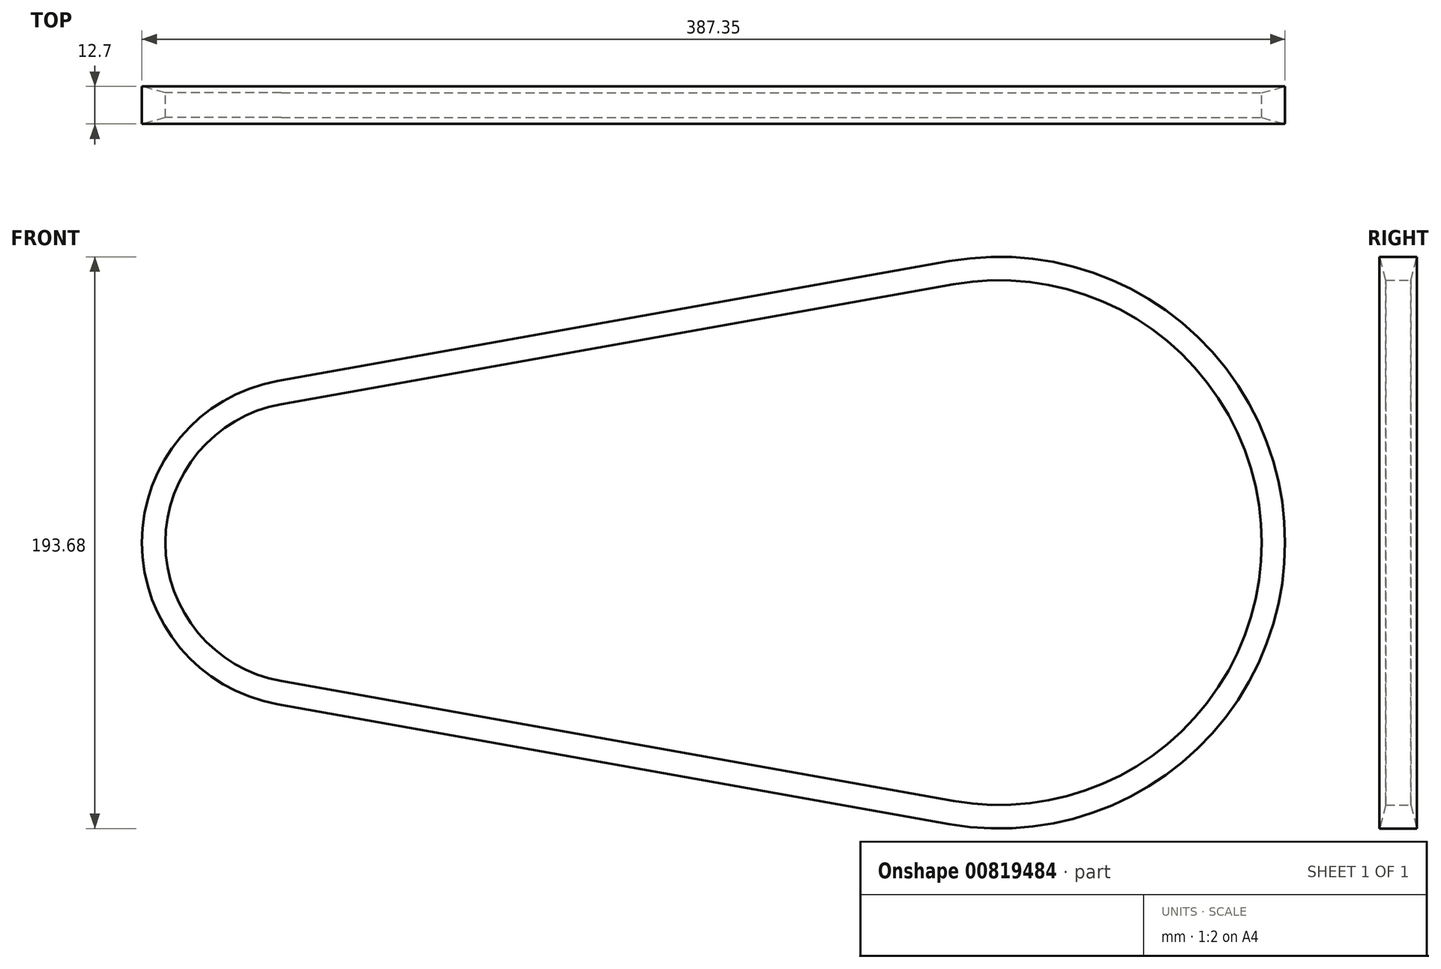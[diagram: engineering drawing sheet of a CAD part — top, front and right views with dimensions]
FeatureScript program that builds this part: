
annotation { "Feature Type Name" : "Feature", "Feature Type Description" : "" }
export const myFeature = defineFeature(function(context is Context, id is Id, definition is map)
    precondition{}
    {
        {
            var Q0;
            Q0=qCreatedBy(makeId("Front.planeOp"),FACE);
            var sketch = newSketch(context, id + "F0", { "sketchPlane" : qUnion([Q0])});
            skArc(sketch, "E0", {"start": v(-15.62, -87.52) * mm, "mid": v(88.9, 0) * mm, "end": v(-15.62, 87.52) * mm});
            skArc(sketch, "E1", {"start": v(-243.32, 46.88) * mm, "mid": v(-282.58, 0) * mm, "end": v(-243.32, -46.88) * mm});
            skLineSegment(sketch, "E2", {"start": v(-198.56, 30.72) * mm, "end": v(-176.73, 4.86) * mm, "construction": true});
            skLineSegment(sketch, "E3", {"start": v(-15.62, -87.52) * mm, "end": v(-243.32, -46.88) * mm});
            skArc(sketch, "E4", {"start": v(-176.73, 4.86) * mm, "mid": v(-154.6, -6.36) * mm, "end": v(-131.12, 1.71) * mm, "construction": true});
            skLineSegment(sketch, "E5.trimOffspring", {"start": v(-131.12, 1.71) * mm, "end": v(-59.4, 66.13) * mm, "construction": true});
            skLineSegment(sketch, "E6", {"start": v(-243.32, 46.88) * mm, "end": v(-15.62, 87.52) * mm});
            skSolve(sketch);
        }
        {
            var Q0;
            Q0=sQuery(id+"F0.wireOp",EDGE,"E3");
            cPoint(context, id + "F1", {"entities" : qUnion([Q0]), "parameter" : 0.5});
        }
        {
            var Q0;
            Q0=qCreatedBy(id+"F1",VERTEX);
            var Q1;
            Q1=sQuery(id+"F0.wireOp",EDGE,"E3");
            cPlane(context, id + "F2", {"entities" : qUnion([Q0, Q1]), "cplaneType" : CPlaneType.CURVE_POINT, "offset" : 25.4 * mm, "width" : 152.4 * mm, "height" : 152.4 * mm});
        }
        {
            var Q0;
            Q0=qCreatedBy(id+"F2.planeOp",FACE);
            var sketch = newSketch(context, id + "F3", { "sketchPlane" : qUnion([Q0])});
            skLineSegment(sketch, "E7", {"start": v(6.35, -96.84) * mm, "end": v(-6.35, -96.84) * mm});
            skLineSegment(sketch, "E8", {"start": v(-6.35, -96.84) * mm, "end": v(-4.22, -88.9) * mm});
            skLineSegment(sketch, "E9", {"start": v(-4.22, -88.9) * mm, "end": v(4.22, -88.9) * mm});
            skLineSegment(sketch, "E10", {"start": v(4.22, -88.9) * mm, "end": v(6.35, -96.84) * mm});
            skLineSegment(sketch, "E11", {"start": v(0, -88.9) * mm, "end": v(0, -96.84) * mm, "construction": true});
            skPoint(sketch, "E11.startSnap0", {"position": v(0, -96.84) * mm});
            skSolve(sketch);
        }
        {
            var Q0;
            Q0=qSketchRegion(id+"F3",true);
            var Q1;
            Q1=qConstructionFilter(qBodyType(qCreatedBy(id+"F0",EDGE),BodyType.WIRE),ConstructionObject.NO);
            sweep(context, id + "F4", {"profiles" : qUnion([Q0]), "path" : qUnion([Q1])});
        }
    });
